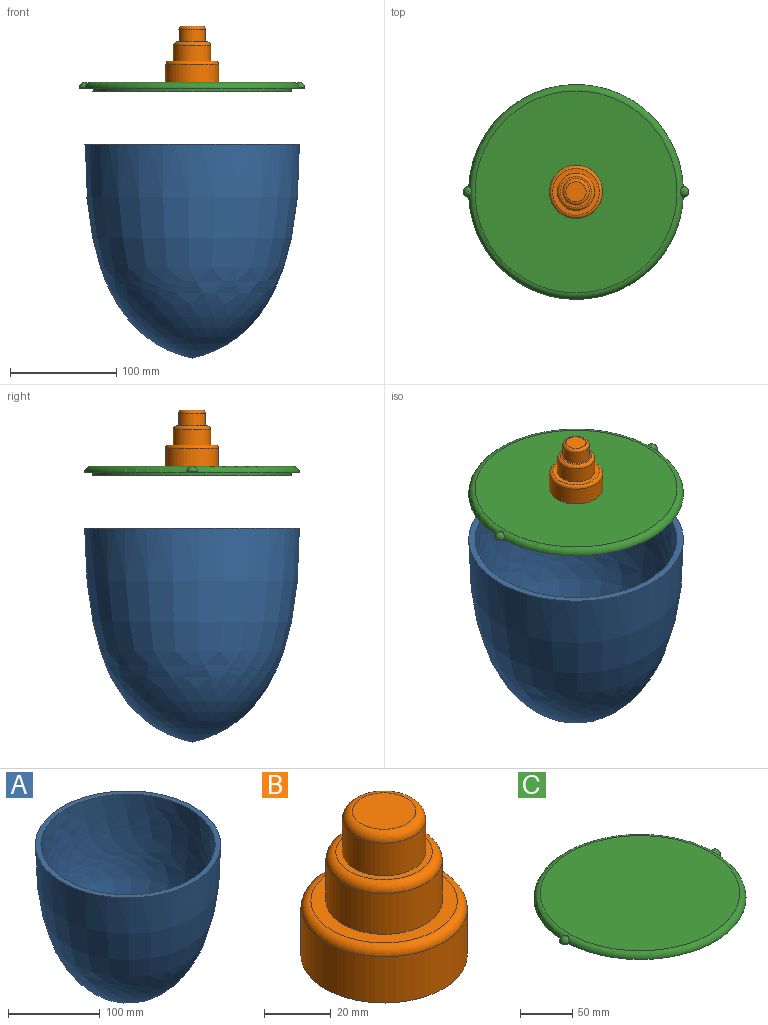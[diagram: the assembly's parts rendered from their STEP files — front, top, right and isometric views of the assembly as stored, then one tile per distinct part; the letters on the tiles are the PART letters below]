
ASSEMBLY  parts=3 mates=2
PART A: 3 faces, bbox 202x202x201 mm
  f0: revolved ~195x190mm, area 100260.5mm2, adj f2
  f1: revolved ~202x202mm, area 111859.4mm2, adj f2
  f2: plane 202x202mm, normal (0,0,1), area 3694.5mm2, adj f0,f1
PART B: 10 faces, bbox 54.1x54.1x53 mm
  f0: cylinder r=25mm len=50mm, axis (0,0,-1), area 2670.4mm2, adj f2,f9
  f1: plane 44x44mm, normal (0,0,1), area 558.4mm2, adj f3,f9
  f2: plane 50x50mm, normal (0,0,-1), area 1963.5mm2, adj f0
  f3: cylinder r=17.5mm len=35mm, axis (0,0,-1), area 1649.3mm2, adj f1,f8
  f4: plane 29x29mm, normal (0,0,1), area 169.6mm2, adj f5,f8
  f5: cylinder r=12.5mm len=25mm, axis (0,0,-1), area 942.5mm2, adj f4,f7
  f6: plane 19x19mm, normal (0,0,1), area 283.5mm2, adj f7
  f7: torus R=9.5mm, axis (0,0,1), area 337.8mm2, adj f5,f6
  f8: torus R=14.5mm, axis (0,0,1), area 485.9mm2, adj f3,f4
  f9: torus R=22mm, axis (0,0,1), area 707.9mm2, adj f0,f1
PART C: 11 faces, bbox 218.6x218.6x9 mm
  f0: cylinder r=90mm len=180mm, axis (0,0,-1), area 1696.5mm2, adj f2,f7
  f1: cylinder r=93.5mm len=187mm, axis (0,0,-1), area 1762.4mm2, adj f2,f3
  f2: plane 187x187mm, normal (0,0,-1), area 2017.7mm2, adj f0,f1
  f3: plane 212x202mm, normal (0,0,-1), area 4662.2mm2, adj f1,f5,f6,f10
  f4: plane 190x190mm, normal (0,0,1), area 28352.9mm2, adj f10
  f5: cylinder r=5mm len=10mm, axis (0,0,-1), area 16mm2, adj f3,f9,f10
  f6: cylinder r=5mm len=10mm, axis (0,0,-1), area 16mm2, adj f3,f8,f10
  f7: plane 180x180mm, normal (0,0,-1), area 25446.9mm2, adj f0
  f8: sphere r=5mm, area 105.5mm2, adj f6,f10
  f9: sphere r=5mm, area 105.5mm2, adj f5,f10
  f10: torus R=95mm, axis (0,0,1), area 5752.7mm2, adj f3,f4,f5,f6,f8,f9
PLACE A t=(-543.45,71.87,342.84)mm
PLACE B t=(-341.43,71.87,493.28)mm
PLACE C t=(-341.43,71.87,484.28)mm
MATE slider A.f2 <-> C.f0  axis (0,0,1) through (-341.43,71.87,435)mm
MATE fastened B.f0 <-> C.f10  axis (0,0,-1) through (-341.43,71.87,493.28)mm
